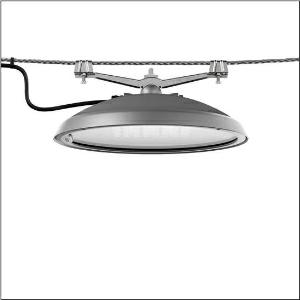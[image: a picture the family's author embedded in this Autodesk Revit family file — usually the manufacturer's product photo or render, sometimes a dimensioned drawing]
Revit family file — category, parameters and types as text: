
# Revit family: dl_r__50_iq_mini___st1_0s_5xa248w31f08re_8883
name_source: partatom
category: Lighting Fixtures
units: mm (PartAtom-declared; Revit-internal decimal feet)

## family parameters
Cut with Voids When Loaded = No
Host = Face
Light Source = No
Part Type = Normal
Room Calculation Point = No
Round Connector Dimension = Use Diameter
Shared = No

## types (1)
- --- (1 x LED, 6000 lm, 35.4 W, 3000K)
    Apparent Load = 35 VA
    CIE Flux Codes = 37 72 97 100 100
    Color Rendering = 70
    Color Temperature = 3000K
    Default Elevation = 1800 mm
    Description = DL® 50 iQ mini, catenary luminaire, primary light control with lens, of PMMA, primary optical cover: cover, of toughened safety glass, transparent, light distribution: ST1.0s, light emission: direct distribution, primary light characteristic: symmetric, installation type: suspended mounting, LED, High Power LED, rated luminous flux: 6.000lm, luminous efficacy: 170lm/W, light colour: 730, colour temperature: 3000K, control: optimised constant luminous flux control (CLO 2.0), Desk-Remote (wireless, voltage-free reading and setting of iQ features in the workshop via application-optimized NFC function/RFID function), Light-Fading, Smart-Wire, Night-Set, Lumen-Switch, Temp-Guard, Auto-Match, Street-Remote, mains connection: 230..240V, AC, 50/60Hz, start of lifetime: 35W, end of service life: 36W, reduction: 17W, luminaire housing, of diecast aluminium, powder-coated, Siteco® metallic grey (DB 702S), diameter: 500mm, height: 115mm, protection rating (complete): IP66, insulation class (complete): insulation class II (safety insulation), certification: CE, ENEC, VDE, impact resistance: IK08, permissible operating ambient temperature for outdoor applications: -25..+40°C, standard-compliant lighting for roads and squares, packaging unit: 1 piece

Light Distribution: ST1.0s
    Height = 124 mm  [stored 0.406824 ft]
    Lamp = 1 x LED
    Lamp Light Flux = 6000 lm
    Lamp Power = 35.4 W
    Lamp count = 1
    Length = 500 mm
    Luminous efficacy = 169 lm/W
    Manufacturer = Siteco
    ModVariant = No
    Model = 5XA248W31F08RE
    Number of Poles = 1
    OnlyDefault = Yes
    Power Factor = 1
    Product Name = DL® 50 iQ mini | ST1.0s
    Product group = catenary luminaire
    ProductGroupID = 6300
    Protection Class = Protection class II
    Protection Degree = IP 66
    RLX_Detail_Level = 1
    RLX_Emergency_Light_Flux = 0 lm
    RLX_Emergency_Type = 0
    RLX_Emergency_Type_DB = No
    RlxData = <blob elided: 123389 chars, md5=55e3ed66>
    Socket = socket
    Standby Power = 0 W
    System Light Flux = 6000 lm
    System Power = 35 W
    Type Comments = factory setting: luminous flux: 100 % | dim-lin: 254 | 376 mA
    Type Image = l_1242791.jpg
    URL = http://relux.com
    VarID = @adj_072079
    Voltage = 0 V
    Weight = 0.00 kg
    Width = 0 mm  [stored 0 ft]

note: [stored X ft] marks values corroborated as IEEE doubles in the binary element streams (Revit-internal decimal feet)

## geometry (parser evidence)
native form markers: Blend x4, Sweep x12
no freeform markers — native parametric forms only
